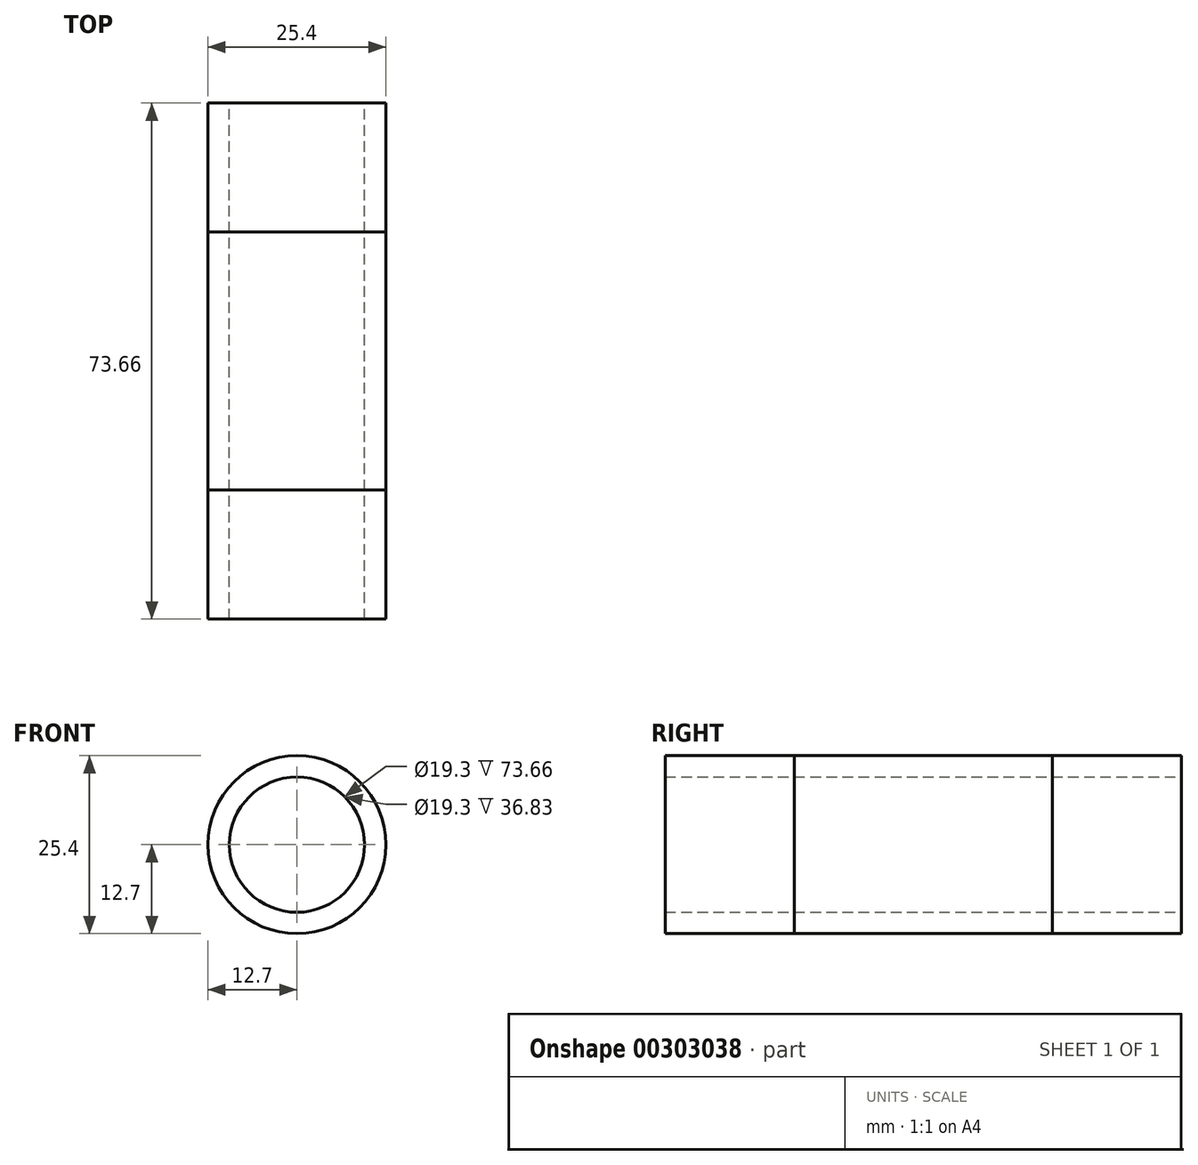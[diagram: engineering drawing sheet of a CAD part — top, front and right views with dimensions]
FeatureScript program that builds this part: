
annotation { "Feature Type Name" : "Feature", "Feature Type Description" : "" }
export const myFeature = defineFeature(function(context is Context, id is Id, definition is map)
    precondition{}
    {
        {
            var Q0;
            Q0=qCreatedBy(makeId("Front.planeOp"),FACE);
            var sketch = newSketch(context, id + "F0", { "sketchPlane" : qUnion([Q0])});
            skCircle(sketch, "E0", {"center": v(0, 0) * mm, "radius": 12.7 * mm});
            skCircle(sketch, "E1", {"center": v(0, 0) * mm, "radius": 9.65 * mm});
            skSolve(sketch);
        }
        {
            var Q0;
            Q0=makeQuery(id+"F0.imprint","IMPRINT",FACE,{"disambiguationData":[TD([[makeQuery(id+"F0.imprint","IMPRINT",EDGE,{"derivedFrom":sQuery(id+"F0.wireOp",EDGE,"E0")}),1.0]])]});
            extrude(context, id + "F1", {"entities" : qUnion([Q0]), "depth" : 36.83 * mm, "symmetric" : true});
        }
        {
            var Q0;
            Q0=makeQuery(id+"F0.imprint","IMPRINT",FACE,{"disambiguationData":[TD([[makeQuery(id+"F0.imprint","IMPRINT",EDGE,{"derivedFrom":sQuery(id+"F0.wireOp",EDGE,"E0")}),1.0]])]});
            extrude(context, id + "F2", {"entities" : qUnion([Q0]), "depth" : 73.66 * mm, "symmetric" : true});
        }
    });
